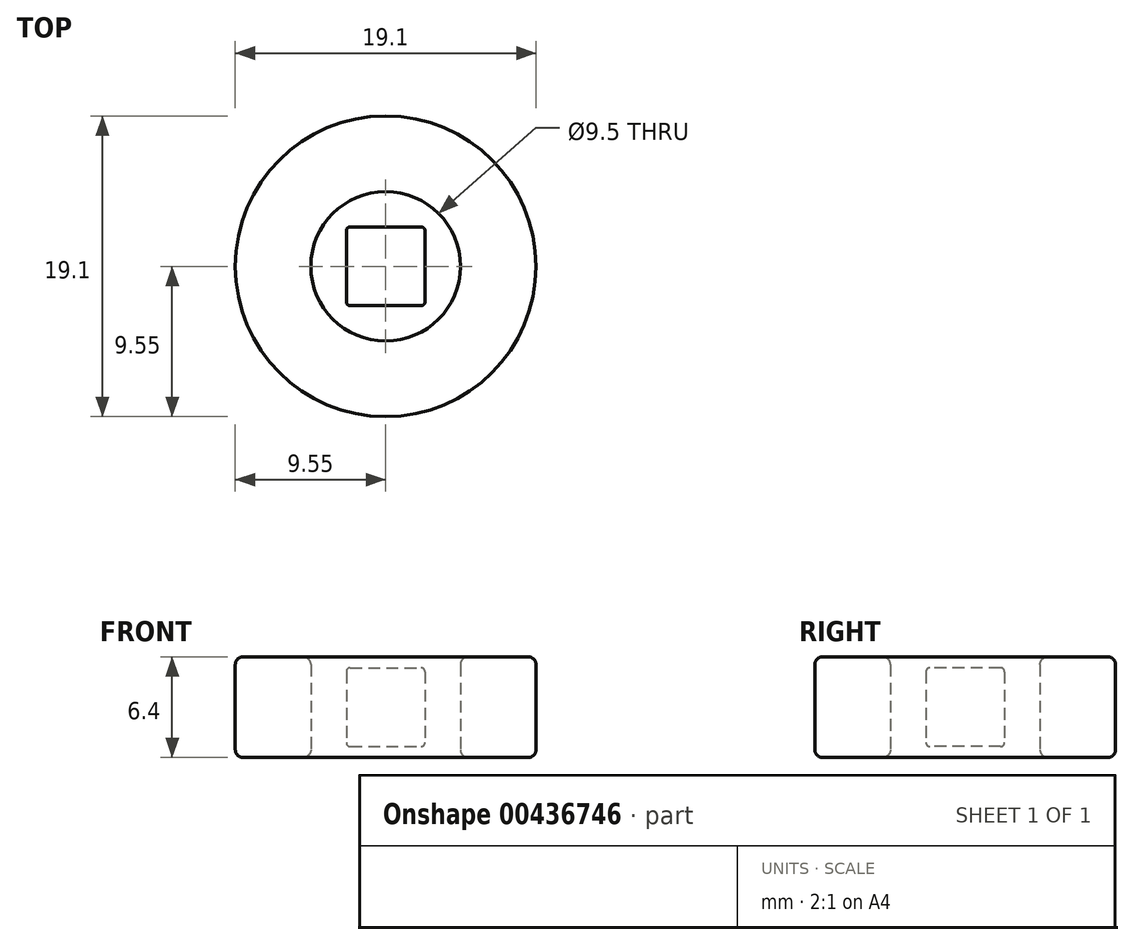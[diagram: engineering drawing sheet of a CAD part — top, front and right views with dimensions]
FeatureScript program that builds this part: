
annotation { "Feature Type Name" : "Feature", "Feature Type Description" : "" }
export const myFeature = defineFeature(function(context is Context, id is Id, definition is map)
    precondition{}
    {
        {
            var Q0;
            Q0=qCreatedBy(makeId("Top.planeOp"),FACE);
            var sketch = newSketch(context, id + "F0", { "sketchPlane" : qUnion([Q0])});
            skLineSegment(sketch, "E0", {"start": v(0, 3.17) * mm, "end": v(0, -3.29) * mm, "construction": true});
            skLineSegment(sketch, "E1", {"start": v(-3.64, 0) * mm, "end": v(3.1, 0) * mm, "construction": true});
            skLineSegment(sketch, "E2.bottom", {"start": v(-2.5, 2.5) * mm, "end": v(2.5, 2.5) * mm});
            skLineSegment(sketch, "E2.top", {"start": v(-2.5, -2.5) * mm, "end": v(2.5, -2.5) * mm});
            skLineSegment(sketch, "E2.left", {"start": v(-2.5, 2.5) * mm, "end": v(-2.5, -2.5) * mm});
            skLineSegment(sketch, "E2.right", {"start": v(2.5, 2.5) * mm, "end": v(2.5, -2.5) * mm});
            skSolve(sketch);
        }
        {
            var Q0;
            Q0 = qSketchRegion(id + "F0", true);
            extrude(context, id + "F1", {"entities" : qUnion([Q0]), "depth" : 5 * mm, "offsetDistance" : 25 * mm, "symmetric" : true});
        }
        {
            var Q0;
            Q0=makeQuery(id+"F1.opExtrude","SWEPT_EDGE",EDGE,{"disambiguationData":[OSD([sQuery(id+"F0.wireOp",EDGE,"E2.bottom"),sQuery(id+"F0.wireOp",EDGE,"E2.right")])]});
            var Q1;
            Q1=makeQuery(id+"F1.opExtrude","SWEPT_EDGE",EDGE,{"disambiguationData":[OSD([sQuery(id+"F0.wireOp",EDGE,"E2.top"),sQuery(id+"F0.wireOp",EDGE,"E2.right")])]});
            var Q2;
            Q2=makeQuery(id+"F1.opExtrude","SWEPT_EDGE",EDGE,{"disambiguationData":[OSD([sQuery(id+"F0.wireOp",EDGE,"E2.top"),sQuery(id+"F0.wireOp",EDGE,"E2.left")])]});
            var Q3;
            Q3=makeQuery(id+"F1.opExtrude","SWEPT_EDGE",EDGE,{"disambiguationData":[OSD([sQuery(id+"F0.wireOp",EDGE,"E2.bottom"),sQuery(id+"F0.wireOp",EDGE,"E2.left")])]});
            var Q4;
            Q4=makeQuery(id+"F1.opExtrude","CAP_EDGE",EDGE,{"disambiguationData":[OSD([sQuery(id+"F0.wireOp",EDGE,"E2.left")])],"isStart":false});
            var Q5;
            Q5=makeQuery(id+"F1.opExtrude","CAP_EDGE",EDGE,{"disambiguationData":[OSD([sQuery(id+"F0.wireOp",EDGE,"E2.left")])],"isStart":true});
            var Q6;
            Q6=makeQuery(id+"F1.opExtrude","CAP_EDGE",EDGE,{"disambiguationData":[OSD([sQuery(id+"F0.wireOp",EDGE,"E2.top")])],"isStart":false});
            var Q7;
            Q7=makeQuery(id+"F1.opExtrude","CAP_EDGE",EDGE,{"disambiguationData":[OSD([sQuery(id+"F0.wireOp",EDGE,"E2.right")])],"isStart":false});
            var Q8;
            Q8=makeQuery(id+"F1.opExtrude","CAP_EDGE",EDGE,{"disambiguationData":[OSD([sQuery(id+"F0.wireOp",EDGE,"E2.bottom")])],"isStart":false});
            var Q9;
            Q9=makeQuery(id+"F1.opExtrude","CAP_EDGE",EDGE,{"disambiguationData":[OSD([sQuery(id+"F0.wireOp",EDGE,"E2.top")])],"isStart":true});
            var Q10;
            Q10=makeQuery(id+"F1.opExtrude","CAP_EDGE",EDGE,{"disambiguationData":[OSD([sQuery(id+"F0.wireOp",EDGE,"E2.right")])],"isStart":true});
            var Q11;
            Q11=makeQuery(id+"F1.opExtrude","CAP_EDGE",EDGE,{"disambiguationData":[OSD([sQuery(id+"F0.wireOp",EDGE,"E2.bottom")])],"isStart":true});
            fillet(context, id + "F2", {"entities" : qUnion([Q0, Q1, Q2, Q3, Q4, Q5, Q6, Q7, Q8, Q9, Q10, Q11]), "radius" : 0.25 * mm, "tangentPropagation" : true, "allowEdgeOverflow" : false});
        }
        {
            var Q0;
            Q0=qCreatedBy(makeId("Top.planeOp"),FACE);
            var sketch = newSketch(context, id + "F3", { "sketchPlane" : qUnion([Q0])});
            skCircle(sketch, "E3", {"center": v(0, 0) * mm, "radius": 9.55 * mm});
            skCircle(sketch, "E4", {"center": v(0, 0) * mm, "radius": 4.75 * mm});
            skSolve(sketch);
        }
        {
            var Q0;
            Q0 = qSketchRegion(id + "F3", true);
            extrude(context, id + "F4", {"entities" : qUnion([Q0]), "depth" : 6.4 * mm, "offsetDistance" : 25 * mm, "symmetric" : true});
        }
        {
            var Q0;
            Q0=makeQuery(id+"F4.opExtrude","CAP_EDGE",EDGE,{"disambiguationData":[OSD([sQuery(id+"F3.wireOp",EDGE,"E3")])],"isStart":false});
            var Q1;
            Q1=makeQuery(id+"F4.opExtrude","CAP_EDGE",EDGE,{"disambiguationData":[OSD([sQuery(id+"F3.wireOp",EDGE,"E3")])],"isStart":true});
            var Q2;
            Q2=makeQuery(id+"F4.opExtrude","CAP_EDGE",EDGE,{"disambiguationData":[OSD([sQuery(id+"F3.wireOp",EDGE,"E4")])],"isStart":false});
            var Q3;
            Q3=makeQuery(id+"F4.opExtrude","CAP_EDGE",EDGE,{"disambiguationData":[OSD([sQuery(id+"F3.wireOp",EDGE,"E4")])],"isStart":true});
            fillet(context, id + "F5", {"entities" : qUnion([Q0, Q1, Q2, Q3]), "radius" : 0.5 * mm, "tangentPropagation" : true, "allowEdgeOverflow" : false});
        }
    });
